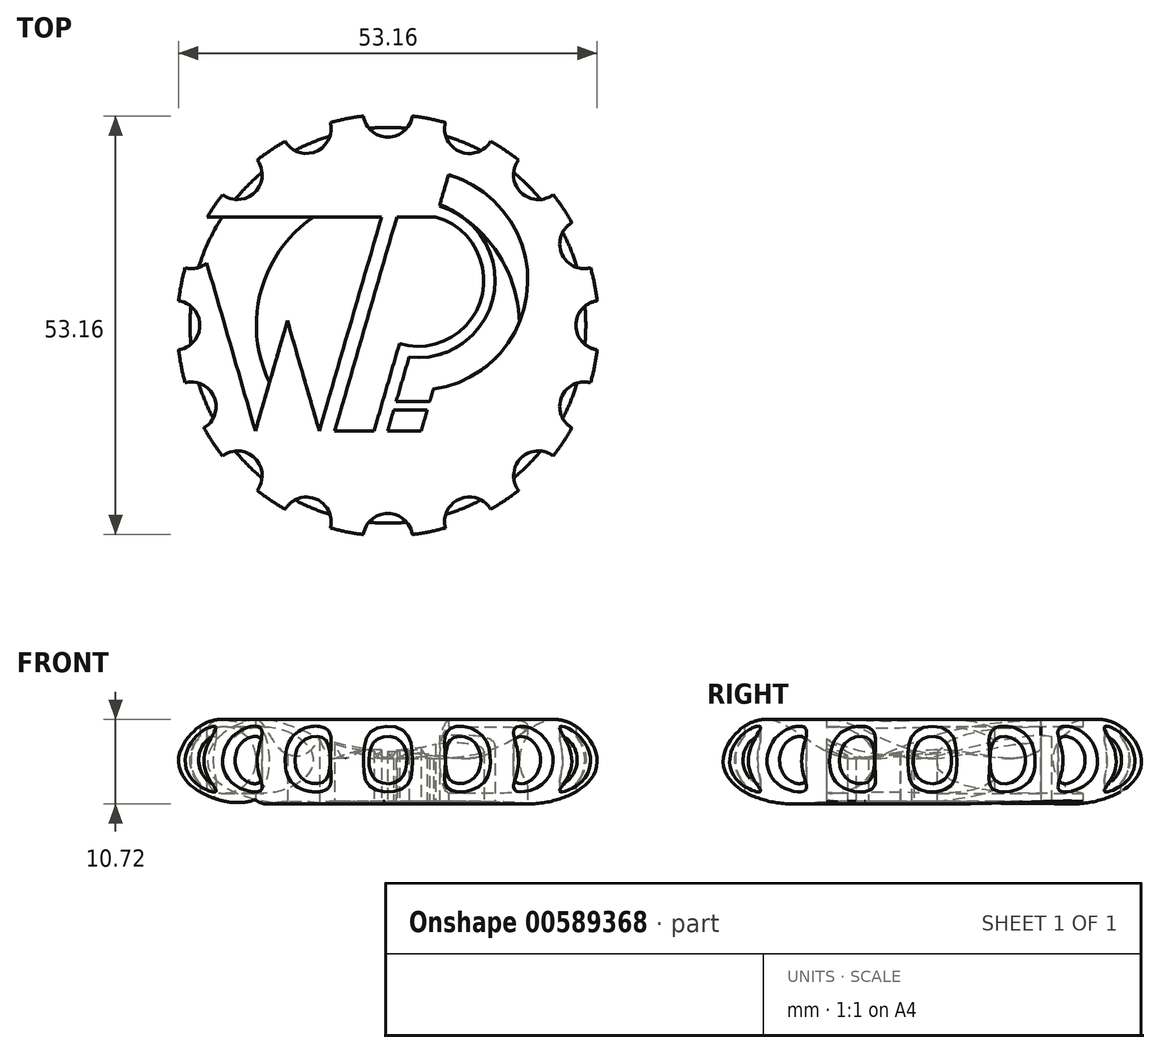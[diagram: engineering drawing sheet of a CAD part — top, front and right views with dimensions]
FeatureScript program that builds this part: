
annotation { "Feature Type Name" : "Feature", "Feature Type Description" : "" }
export const myFeature = defineFeature(function(context is Context, id is Id, definition is map)
    precondition{}
    {
        {
            var Q0;
            Q0=qCreatedBy(makeId("Front.planeOp"),FACE);
            var sketch = newSketch(context, id + "F0", { "sketchPlane" : qUnion([Q0])});
            skFitSpline(sketch, "E0", {"points": [v(0, 0) * mm, v(-13.8, 0) * mm, v(-20.16, 0) * mm, v(-25.9, 2.9) * mm, v(-26.36, 6.93) * mm, v(-21.56, 10.5) * mm, v(-15.97, 8.01) * mm, v(-11.32, 5.69) * mm, v(-6.51, 6) * mm, v(0, 7.08) * mm], "startDerivative": vector(-93.44, 1.73) * mm, "endDerivative": vector(59.59, 9.72) * mm});
            skLineSegment(sketch, "E1", {"start": v(0, 20.11) * mm, "end": v(0, -5.94) * mm, "construction": true});
            skLineSegment(sketch, "E2", {"start": v(0, 7.08) * mm, "end": v(0, 0) * mm});
            skCircle(sketch, "E3", {"center": v(-20.92, 5.35) * mm, "radius": 4.22 * mm});
            skSolve(sketch);
        }
        {
            var Q0;
            Q0 = qSketchRegion(id + "F0", true);
            var Q1;
            Q1=sQuery(id+"F0.wireOp",EDGE,"E1");
            revolve(context, id + "F1", {"entities" : qUnion([Q0]), "axis" : qUnion([Q1]), "revolveType" : RevolveType.FULL});
        }
        {
            var Q0;
            Q0=qCreatedBy(makeId("Top.planeOp"),FACE);
            var sketch = newSketch(context, id + "F2", { "sketchPlane" : qUnion([Q0])});
            skLineSegment(sketch, "E4", {"start": v(-24.7, 13.77) * mm, "end": v(-16.83, -13.44) * mm});
            skLineSegment(sketch, "E5", {"start": v(-16.83, -13.44) * mm, "end": v(-12.76, 0.57) * mm});
            skLineSegment(sketch, "E6", {"start": v(-12.76, 0.57) * mm, "end": v(-8.7, -13.44) * mm});
            skLineSegment(sketch, "E7", {"start": v(-8.7, -13.44) * mm, "end": v(-0.8, 13.77) * mm});
            skLineSegment(sketch, "E8", {"start": v(-0.8, 13.77) * mm, "end": v(-24.7, 13.77) * mm});
            skLineSegment(sketch, "E9", {"start": v(1.15, 13.77) * mm, "end": v(-6.76, -13.44) * mm});
            skLineSegment(sketch, "E10", {"start": v(-6.76, -13.44) * mm, "end": v(-1.76, -13.44) * mm});
            skLineSegment(sketch, "E11", {"start": v(-1.76, -13.44) * mm, "end": v(1.46, -2.36) * mm});
            skLineSegment(sketch, "E12", {"start": v(1.46, -2.36) * mm, "end": v(6.15, 13.77) * mm, "construction": true});
            skPoint(sketch, "E12.endSnap0", {"position": v(-12.75, 13.77) * mm});
            skArc(sketch, "E13", {"start": v(1.47, -2.34) * mm, "mid": v(11.87, 3.4) * mm, "end": v(6.08, 13.77) * mm});
            skLineSegment(sketch, "E14", {"start": v(1.15, 13.77) * mm, "end": v(6.08, 13.77) * mm});
            skArc(sketch, "E15", {"start": v(2.7, -4.05) * mm, "mid": v(13.43, 3.77) * mm, "end": v(6.55, 15.13) * mm});
            skArc(sketch, "E16", {"start": v(5.78, -8.11) * mm, "mid": v(17.73, 4.72) * mm, "end": v(7.7, 19.11) * mm});
            skLineSegment(sketch, "E17", {"start": v(2.7, -4.05) * mm, "end": v(1.05, -9.7) * mm});
            skLineSegment(sketch, "E18", {"start": v(-0.04, -13.44) * mm, "end": v(4.23, -13.44) * mm});
            skLineSegment(sketch, "E19", {"start": v(4.23, -13.44) * mm, "end": v(5, -10.78) * mm});
            skLineSegment(sketch, "E20", {"start": v(5, -10.78) * mm, "end": v(0.74, -10.78) * mm});
            skLineSegment(sketch, "E21", {"start": v(1.05, -9.7) * mm, "end": v(5.31, -9.7) * mm});
            skLineSegment(sketch, "E22", {"start": v(6.15, 13.77) * mm, "end": v(10.6, 29.1) * mm, "construction": true});
            skLineSegment(sketch, "E23", {"start": v(7.7, 19.11) * mm, "end": v(6.55, 15.13) * mm});
            skLineSegment(sketch, "E24.trimOffspring", {"start": v(0.74, -10.78) * mm, "end": v(-0.04, -13.44) * mm});
            skLineSegment(sketch, "E25.trimOffspring", {"start": v(5.31, -9.7) * mm, "end": v(5.78, -8.11) * mm});
            skLineSegment(sketch, "E26", {"start": v(1.47, -2.34) * mm, "end": v(1.46, -2.36) * mm});
            skSolve(sketch);
        }
        {
            var Q0;
            Q0=qCreatedBy(makeId("Top.planeOp"),FACE);
            var sketch = newSketch(context, id + "F3", { "sketchPlane" : qUnion([Q0])});
            skCircle(sketch, "E27", {"center": v(0, 27.02) * mm, "radius": 3.14 * mm});
            skCircle(sketch, "E28.1.0", {"center": v(10.34, 24.96) * mm, "radius": 3.14 * mm});
            skCircle(sketch, "E28.2.0", {"center": v(19.1, 19.1) * mm, "radius": 3.14 * mm});
            skCircle(sketch, "E28.3.0", {"center": v(24.96, 10.34) * mm, "radius": 3.14 * mm});
            skCircle(sketch, "E28.4.0", {"center": v(27.02, 0) * mm, "radius": 3.14 * mm});
            skCircle(sketch, "E28.5.0", {"center": v(24.96, -10.34) * mm, "radius": 3.14 * mm});
            skCircle(sketch, "E28.6.0", {"center": v(19.1, -19.1) * mm, "radius": 3.14 * mm});
            skCircle(sketch, "E28.7.0", {"center": v(10.34, -24.96) * mm, "radius": 3.14 * mm});
            skCircle(sketch, "E28.8.0", {"center": v(0, -27.02) * mm, "radius": 3.14 * mm});
            skCircle(sketch, "E28.9.0", {"center": v(-10.34, -24.96) * mm, "radius": 3.14 * mm});
            skCircle(sketch, "E28.10.0", {"center": v(-19.1, -19.1) * mm, "radius": 3.14 * mm});
            skCircle(sketch, "E28.11.0", {"center": v(-24.96, -10.34) * mm, "radius": 3.14 * mm});
            skCircle(sketch, "E28.12.0", {"center": v(-27.02, 0) * mm, "radius": 3.14 * mm});
            skCircle(sketch, "E28.13.0", {"center": v(-24.96, 10.34) * mm, "radius": 3.14 * mm});
            skCircle(sketch, "E28.14.0", {"center": v(-19.1, 19.1) * mm, "radius": 3.14 * mm});
            skCircle(sketch, "E28.15.0", {"center": v(-10.34, 24.96) * mm, "radius": 3.14 * mm});
            skPoint(sketch, "E28.center", {"position": v(0, 0) * mm});
            skLineSegment(sketch, "E28.anchor1", {"start": v(0, 0) * mm, "end": v(0, 27.02) * mm, "construction": true});
            skLineSegment(sketch, "E28.anchor2", {"start": v(0, 0) * mm, "end": v(-10.34, 24.96) * mm, "construction": true});
            skSolve(sketch);
        }
        {
            var Q0;
            Q0 = qSketchRegion(id + "F3", true);
            extrude(context, id + "F4", {"entities" : qUnion([Q0]), "operationType" : NewBodyOperationType.REMOVE, "depth" : 25 * mm, "offsetDistance" : 25 * mm});
        }
        {
            var Q0;
            Q0 = qSketchRegion(id + "F2", true);
            extrude(context, id + "F5", {"entities" : qUnion([Q0]), "operationType" : NewBodyOperationType.REMOVE, "depth" : 25 * mm, "offsetDistance" : 25 * mm, "hasSecondDirection" : true, "secondDirectionOppositeDirection" : true, "secondDirectionDepth" : 25 * mm});
        }
        {
            var Q0;
            Q0=makeQuery(id+"F0.imprint","IMPRINT",FACE,{"disambiguationData":[TD([[makeQuery(id+"F0.imprint","IMPRINT",EDGE,{"derivedFrom":sQuery(id+"F0.wireOp",EDGE,"E3")}),1.0]])]});
            var Q1;
            Q1=sQuery(id+"F0.wireOp",EDGE,"E1");
            revolve(context, id + "F6", {"operationType" : NewBodyOperationType.ADD, "entities" : qUnion([Q0]), "axis" : qUnion([Q1]), "revolveType" : RevolveType.FULL});
        }
    });
